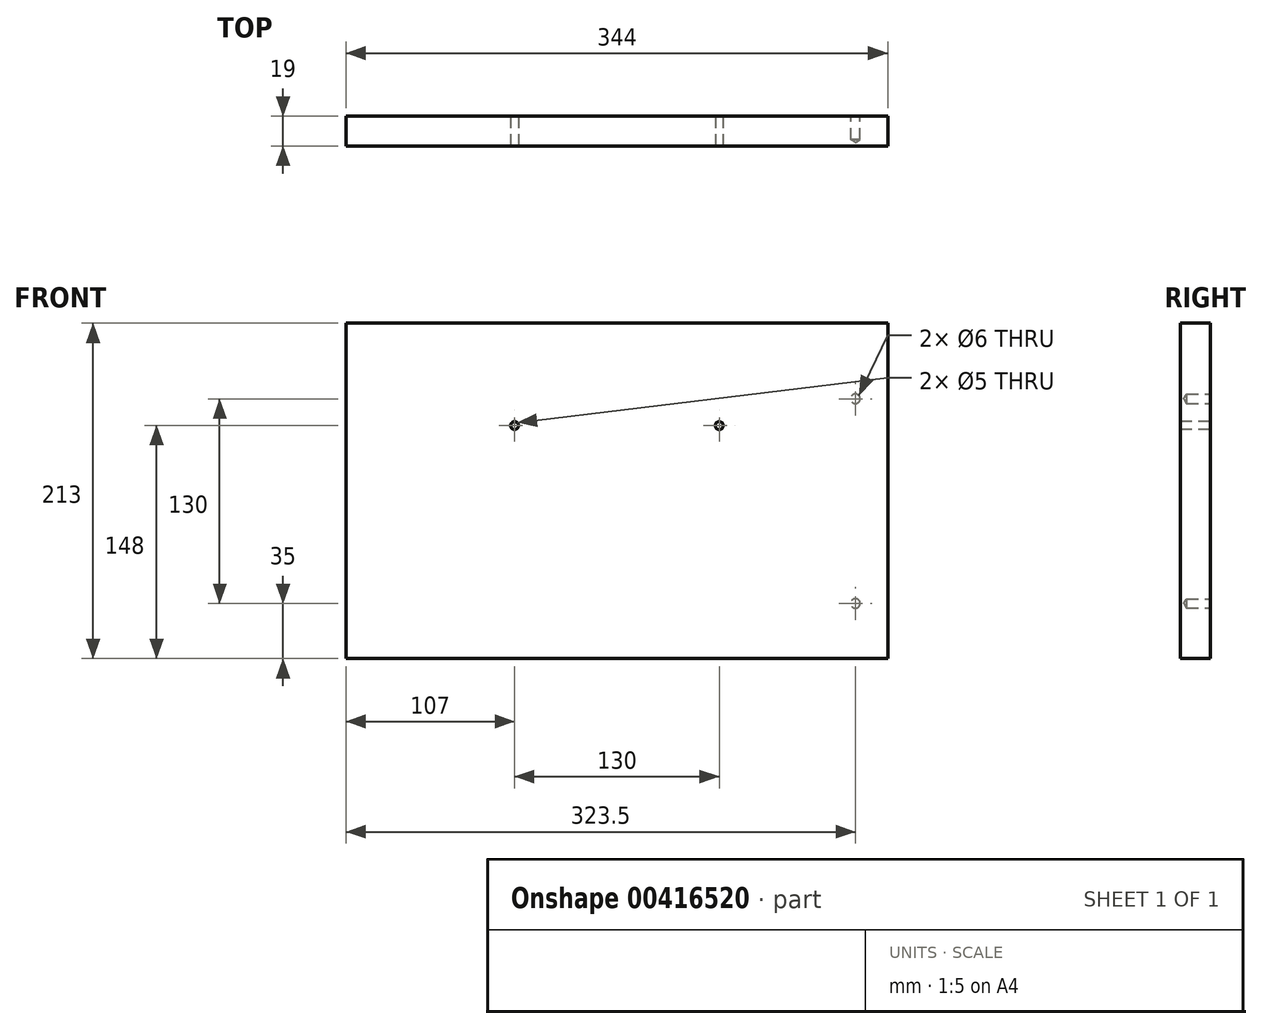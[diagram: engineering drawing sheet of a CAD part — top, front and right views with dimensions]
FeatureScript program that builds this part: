
annotation { "Feature Type Name" : "Feature", "Feature Type Description" : "" }
export const myFeature = defineFeature(function(context is Context, id is Id, definition is map)
    precondition{}
    {
        {
            var Q0;
            Q0=qCreatedBy(makeId("Front.planeOp"),FACE);
            var sketch = newSketch(context, id + "F0", { "sketchPlane" : qUnion([Q0])});
            skLineSegment(sketch, "E0.bottom", {"start": v(-172, 106.5) * mm, "end": v(172, 106.5) * mm});
            skLineSegment(sketch, "E0.top", {"start": v(-172, -106.5) * mm, "end": v(172, -106.5) * mm});
            skLineSegment(sketch, "E0.left", {"start": v(-172, 106.5) * mm, "end": v(-172, -106.5) * mm});
            skLineSegment(sketch, "E0.right", {"start": v(172, 106.5) * mm, "end": v(172, -106.5) * mm});
            skPoint(sketch, "E0.middle", {"position": v(0, 0) * mm});
            skSolve(sketch);
        }
        {
            var Q0;
            Q0 = qSketchRegion(id + "F0", true);
            extrude(context, id + "F1", {"entities" : qUnion([Q0]), "depth" : 19 * mm});
        }
        {
            var Q0;
            Q0=makeQuery(id+"F1.opExtrude","CAP_FACE",FACE,{"disambiguationData":[OSD([sQuery(id+"F0.wireOp",EDGE,"E0.bottom"),sQuery(id+"F0.wireOp",EDGE,"E0.top"),sQuery(id+"F0.wireOp",EDGE,"E0.left"),sQuery(id+"F0.wireOp",EDGE,"E0.right")])],"isStart":true});
            var sketch = newSketch(context, id + "F2", { "sketchPlane" : qUnion([Q0])});
            skLineSegment(sketch, "E1", {"start": v(-151.5, 95.65) * mm, "end": v(-151.5, -93.61) * mm, "construction": true});
            skPoint(sketch, "E2", {"position": v(-151.5, 58.5) * mm});
            skPoint(sketch, "E3", {"position": v(-151.5, -71.5) * mm});
            skSolve(sketch);
        }
        {
            var Q0;
            Q0=sQuery(id+"F2.wireOp",VERTEX,"E2");
            var Q1;
            Q1=sQuery(id+"F2.wireOp",VERTEX,"E3");
            var Q2;
            Q2=makeQuery(id+"F1.opExtrude","SWEPT_BODY",BODY,{"disambiguationData":[OSD([sQuery(id+"F0.wireOp",EDGE,"E0.bottom"),sQuery(id+"F0.wireOp",EDGE,"E0.top"),sQuery(id+"F0.wireOp",EDGE,"E0.left"),sQuery(id+"F0.wireOp",EDGE,"E0.right")])]});
            hole(context, id + "F3", {"style" : HoleStyle.SIMPLE, "endStyle" : HoleEndStyle.BLIND, "holeDiameter" : 6 * mm, "holeDepth" : 15 * mm, "isTappedThrough" : true, "tappedDepth" : 12 * mm, "tapClearance" : 3, "startFromSketch" : true, "locations" : qUnion([Q0, Q1]), "scope" : qUnion([Q2])});
        }
        {
            var Q0;
            Q0=makeQuery(id+"F1.opExtrude","CAP_FACE",FACE,{"disambiguationData":[OSD([sQuery(id+"F0.wireOp",EDGE,"E0.bottom"),sQuery(id+"F0.wireOp",EDGE,"E0.top"),sQuery(id+"F0.wireOp",EDGE,"E0.left"),sQuery(id+"F0.wireOp",EDGE,"E0.right")])],"isStart":false});
            var sketch = newSketch(context, id + "F4", { "sketchPlane" : qUnion([Q0])});
            skPoint(sketch, "E4", {"position": v(-65, 41.5) * mm});
            skPoint(sketch, "E5", {"position": v(65, 41.5) * mm});
            skLineSegment(sketch, "E6", {"start": v(-65, 41.5) * mm, "end": v(65, 41.5) * mm, "construction": true});
            skSolve(sketch);
        }
        {
            var Q0;
            Q0=sQuery(id+"F4.wireOp",VERTEX,"E4");
            var Q1;
            Q1=sQuery(id+"F4.wireOp",VERTEX,"E5");
            var Q2;
            Q2=makeQuery(id+"F1.opExtrude","SWEPT_BODY",BODY,{"disambiguationData":[OSD([sQuery(id+"F0.wireOp",EDGE,"E0.bottom"),sQuery(id+"F0.wireOp",EDGE,"E0.top"),sQuery(id+"F0.wireOp",EDGE,"E0.left"),sQuery(id+"F0.wireOp",EDGE,"E0.right")])]});
            hole(context, id + "F5", {"style" : HoleStyle.SIMPLE, "endStyle" : HoleEndStyle.THROUGH, "holeDiameter" : 5 * mm, "isTappedThrough" : true, "tappedDepth" : 12 * mm, "tapClearance" : 3, "startFromSketch" : true, "locations" : qUnion([Q0, Q1]), "scope" : qUnion([Q2])});
        }
    });
